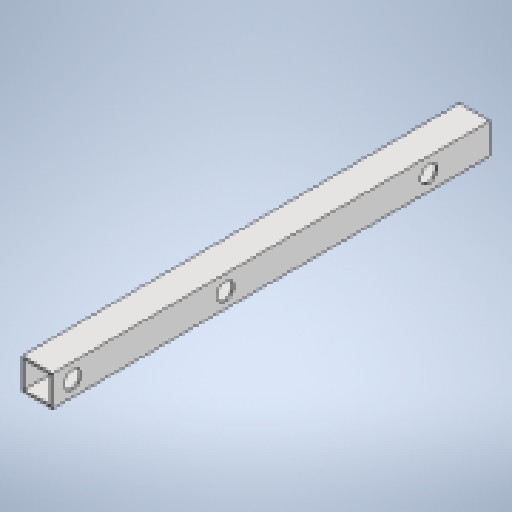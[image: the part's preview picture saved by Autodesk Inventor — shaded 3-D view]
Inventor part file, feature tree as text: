
AUTODESK INVENTOR PART (.ipt)
format: ipt  version: 2025.1 (Build 291241020, 241B)  size: 304,128 bytes
history: native  units: mm
features: extrude x2, sketch x2, projected_geometry x1
ambient origin geometry x8: Origin, YZ Plane, XZ Plane, XY Plane, X Axis, Y Axis, Z Axis, Center Point
bodies: Body1 (feature_tree)
feature tree (5):
  extrude  "Extrusion3"  Depth=30.0mm
  extrude  "Extrusion4"  Depth=2.0mm
  sketch  "Sketch9"  dims[d61=500.0mm d172=30.0mm]
  sketch  "Sketch10"  dims[d173=30.0mm d174=2.0mm d175=420.0mm d176=0.0mm d177=17.0mm d178=17.0mm d179=0.0mm d180=0.0mm d181=30.0mm d182=90.0mm d183=260.0mm d184=435.0mm d185=500.0mm d186=17.0mm]
  projected_geometry  "Projected Loop3"
